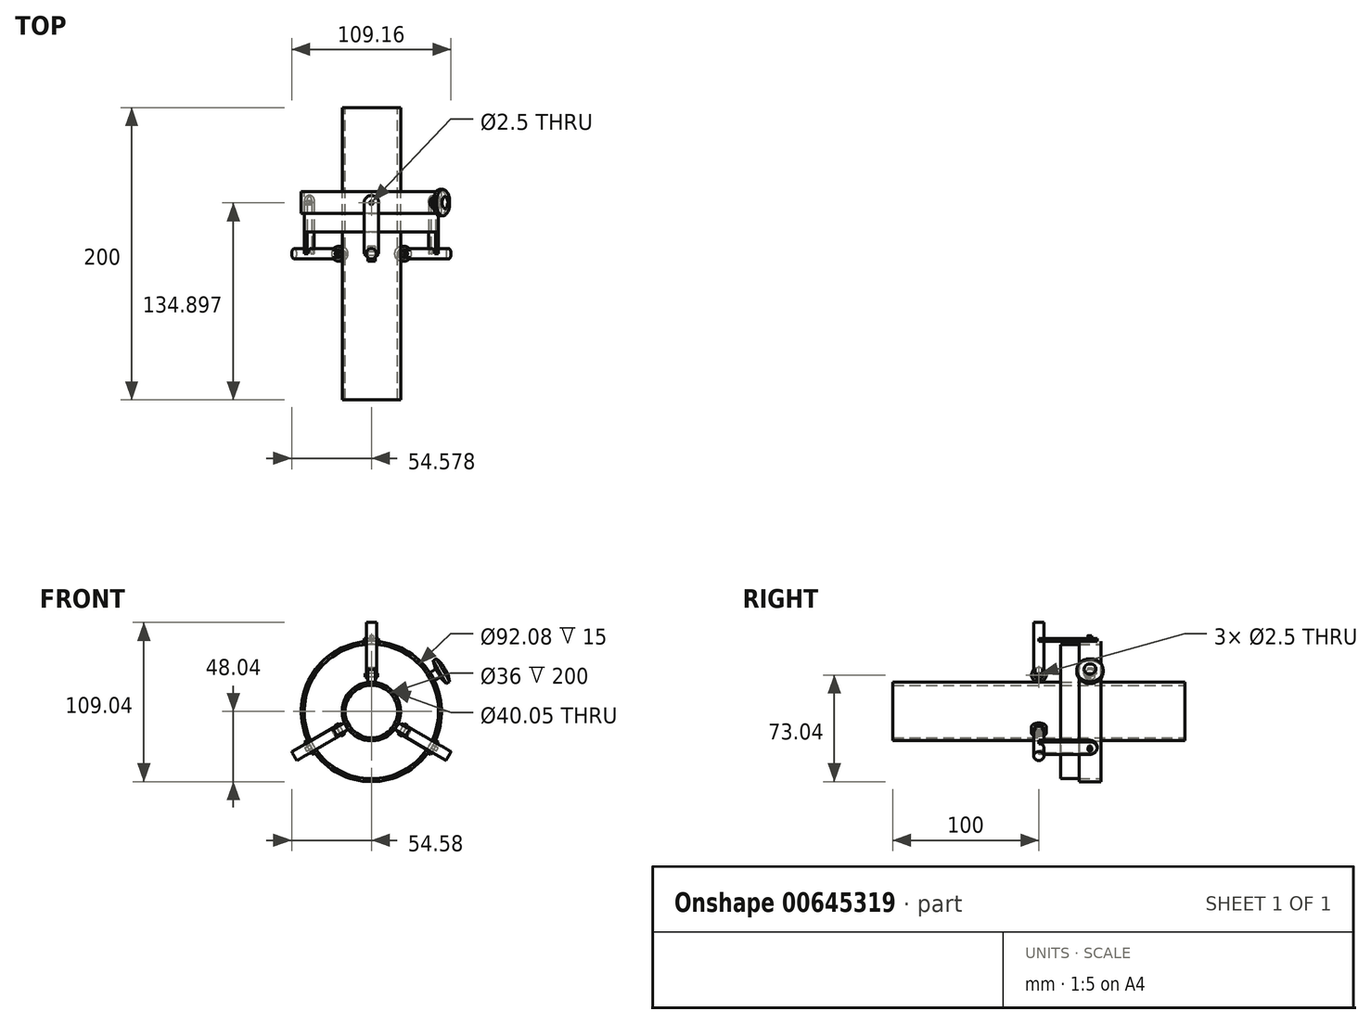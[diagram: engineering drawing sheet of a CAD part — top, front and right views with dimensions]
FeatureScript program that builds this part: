
annotation { "Feature Type Name" : "Feature", "Feature Type Description" : "" }
export const myFeature = defineFeature(function(context is Context, id is Id, definition is map)
    precondition{}
    {
        {
            var Q0;
            Q0=qCreatedBy(makeId("Front.planeOp"),FACE);
            var sketch = newSketch(context, id + "F0", { "sketchPlane" : qUnion([Q0])});
            skCircle(sketch, "E0", {"center": v(0, 0) * mm, "radius": 20 * mm});
            skCircle(sketch, "E1", {"center": v(0, 0) * mm, "radius": 18 * mm});
            skSolve(sketch);
        }
        {
            var Q0;
            Q0 = qSketchRegion(id + "F0", true);
            extrude(context, id + "F1", {"entities" : qUnion([Q0]), "depth" : 200 * mm, "offsetDistance" : 25 * mm, "symmetric" : true});
        }
        {
            var Q0;
            Q0=qCreatedBy(makeId("Right.planeOp"),FACE);
            var sketch = newSketch(context, id + "F2", { "sketchPlane" : qUnion([Q0])});
            skCircle(sketch, "E2", {"center": v(0, 25) * mm, "radius": 5 * mm});
            skCircle(sketch, "E3", {"center": v(0, 25) * mm, "radius": 1.25 * mm});
            skSolve(sketch);
        }
        {
            var Q0;
            Q0 = qSketchRegion(id + "F2", true);
            extrude(context, id + "F3", {"entities" : qUnion([Q0]), "depth" : 5 * mm, "offsetDistance" : 25 * mm, "symmetric" : true});
        }
        {
            var Q0;
            Q0=qCreatedBy(makeId("Right.planeOp"),FACE);
            var sketch = newSketch(context, id + "F4", { "sketchPlane" : qUnion([Q0])});
            skLineSegment(sketch, "E4.bottom", {"start": v(0, 21) * mm, "end": v(0.5, 21) * mm});
            skLineSegment(sketch, "E4.top", {"start": v(0, 61) * mm, "end": v(3.5, 61) * mm});
            skLineSegment(sketch, "E4.left", {"start": v(0, 21) * mm, "end": v(0, 61) * mm});
            skLineSegment(sketch, "E4.right", {"start": v(3.5, 24) * mm, "end": v(3.5, 61) * mm});
            skPoint(sketch, "E5.visualSharp", {"position": v(3.5, 21) * mm});
            skArc(sketch, "E5.filletArc", {"start": v(0.5, 21) * mm, "mid": v(2.62, 21.88) * mm, "end": v(3.5, 24) * mm});
            skSolve(sketch);
        }
        {
            var Q0;
            Q0 = qSketchRegion(id + "F4", true);
            var Q1;
            Q1=sQuery(id+"F4.wireOp",EDGE,"E4.left");
            revolve(context, id + "F5", {"entities" : qUnion([Q0]), "axis" : qUnion([Q1]), "revolveType" : RevolveType.FULL});
        }
        {
            var Q0;
            Q0=makeQuery(id+"F3.opExtrude","SWEPT_BODY",BODY,{"disambiguationData":[OSD([sQuery(id+"F2.wireOp",EDGE,"E2"),sQuery(id+"F2.wireOp",EDGE,"E3")])]});
            var Q1;
            Q1=makeQuery(id+"F5.opRevolve","SWEPT_BODY",BODY,{"disambiguationData":[OSD([sQuery(id+"F4.wireOp",EDGE,"E4.bottom"),sQuery(id+"F4.wireOp",EDGE,"E4.top"),sQuery(id+"F4.wireOp",EDGE,"E4.left"),sQuery(id+"F4.wireOp",EDGE,"E4.right"),sQuery(id+"F4.wireOp",EDGE,"E5.filletArc")])]});
            booleanBodies(context, id + "F6", {"operationType" : BooleanOperationType.SUBTRACTION, "tools" : qUnion([Q0]), "targets" : qUnion([Q1]), "keepTools" : true});
        }
        {
            var Q0;
            Q0=qCreatedBy(makeId("Right.planeOp"),FACE);
            var sketch = newSketch(context, id + "F7", { "sketchPlane" : qUnion([Q0])});
            skCircle(sketch, "E6", {"center": v(0, 25) * mm, "radius": 1.25 * mm});
            skSolve(sketch);
        }
        {
            var Q0;
            Q0 = qSketchRegion(id + "F7", true);
            extrude(context, id + "F8", {"entities" : qUnion([Q0]), "operationType" : NewBodyOperationType.REMOVE, "oppositeDirection" : true, "depth" : 25 * mm, "offsetDistance" : 25 * mm, "symmetric" : true});
        }
        {
            var Q0;
            Q0=qCreatedBy(makeId("Right.planeOp"),FACE);
            var sketch = newSketch(context, id + "F9", { "sketchPlane" : qUnion([Q0])});
            skCircle(sketch, "E7", {"center": v(0, 25) * mm, "radius": 1.25 * mm});
            skSolve(sketch);
        }
        {
            var Q0;
            Q0 = qSketchRegion(id + "F9", true);
            extrude(context, id + "F10", {"entities" : qUnion([Q0]), "depth" : 8.5 * mm, "offsetDistance" : 25 * mm, "symmetric" : true});
        }
        {
            var Q0;
            Q0=qCreatedBy(makeId("Front.planeOp"),FACE);
            var sketch = newSketch(context, id + "F11", { "sketchPlane" : qUnion([Q0])});
            skLineSegment(sketch, "E8.bottom", {"start": v(5, 50.04) * mm, "end": v(-5, 50.04) * mm});
            skLineSegment(sketch, "E8.top", {"start": v(5, 48.04) * mm, "end": v(-5, 48.04) * mm});
            skLineSegment(sketch, "E8.left", {"start": v(5, 50.04) * mm, "end": v(5, 48.04) * mm});
            skLineSegment(sketch, "E8.right", {"start": v(-5, 50.04) * mm, "end": v(-5, 48.04) * mm});
            skSolve(sketch);
        }
        {
            var Q0;
            Q0 = qSketchRegion(id + "F11", true);
            extrude(context, id + "F12", {"entities" : qUnion([Q0]), "operationType" : NewBodyOperationType.ADD, "oppositeDirection" : true, "depth" : 40 * mm, "offsetDistance" : 25 * mm});
        }
        {
            var Q0;
            Q0=makeQuery(id+"F12.opExtrude","SWEPT_FACE",FACE,{"disambiguationData":[OSD([sQuery(id+"F11.wireOp",EDGE,"E8.bottom")])]});
            var sketch = newSketch(context, id + "F13", { "sketchPlane" : qUnion([Q0])});
            skArc(sketch, "E9", {"start": v(5, 34.9) * mm, "mid": v(-0.1, 39.9) * mm, "end": v(-5, 34.72) * mm});
            skLineSegment(sketch, "E10", {"start": v(-5, 34.72) * mm, "end": v(-6.25, 34.72) * mm});
            skLineSegment(sketch, "E11", {"start": v(-6.25, 34.72) * mm, "end": v(-6.25, 41.57) * mm});
            skLineSegment(sketch, "E12", {"start": v(-6.25, 41.57) * mm, "end": v(6.15, 41.57) * mm});
            skLineSegment(sketch, "E13", {"start": v(6.15, 41.57) * mm, "end": v(6.15, 34.9) * mm});
            skLineSegment(sketch, "E14", {"start": v(6.15, 34.9) * mm, "end": v(5, 34.9) * mm});
            skCircle(sketch, "E15", {"center": v(0, 34.9) * mm, "radius": 1.25 * mm});
            skSolve(sketch);
        }
        {
            var Q0;
            Q0 = qSketchRegion(id + "F13", true);
            extrude(context, id + "F14", {"entities" : qUnion([Q0]), "operationType" : NewBodyOperationType.REMOVE, "oppositeDirection" : true, "depth" : 25 * mm, "offsetDistance" : 25 * mm});
        }
        {
            var Q0;
            Q0=makeQuery(id+"F3.opExtrude","SWEPT_BODY",BODY,{"disambiguationData":[OSD([sQuery(id+"F2.wireOp",EDGE,"E2"),sQuery(id+"F2.wireOp",EDGE,"E3")])]});
            var Q1;
            Q1=makeQuery(id+"F5.opRevolve","SWEPT_BODY",BODY,{"disambiguationData":[OSD([sQuery(id+"F4.wireOp",EDGE,"E4.bottom"),sQuery(id+"F4.wireOp",EDGE,"E4.top"),sQuery(id+"F4.wireOp",EDGE,"E4.left"),sQuery(id+"F4.wireOp",EDGE,"E4.right"),sQuery(id+"F4.wireOp",EDGE,"E5.filletArc")])]});
            var Q2;
            Q2=makeQuery(id+"F10.opExtrude","SWEPT_BODY",BODY,{"disambiguationData":[OSD([sQuery(id+"F9.wireOp",EDGE,"E7")])]});
            var Q3;
            Q3=makeQuery(id+"F1.opExtrude","CAP_EDGE",EDGE,{"disambiguationData":[OSD([sQuery(id+"F0.wireOp",EDGE,"E1")])],"isStart":false});
            circularPattern(context, id + "F15", {"entities" : qUnion([Q0, Q1, Q2]), "axis" : qUnion([Q3]), "angle" : 360 * degree, "instanceCount" : 3, "equalSpace" : true});
        }
        {
            var Q0;
            Q0=qCreatedBy(makeId("Front.planeOp"),FACE);
            cPlane(context, id + "F16", {"entities" : qUnion([Q0]), "cplaneType" : CPlaneType.OFFSET, "offset" : 35 * mm, "oppositeDirection" : true, "width" : 150 * mm, "height" : 150 * mm});
        }
        {
            var Q0;
            Q0=qCreatedBy(id+"F16.planeOp",FACE);
            var sketch = newSketch(context, id + "F17", { "sketchPlane" : qUnion([Q0])});
            skCircle(sketch, "E16", {"center": v(0, 0) * mm, "radius": 48.04 * mm});
            skCircle(sketch, "E17", {"center": v(0, 0) * mm, "radius": 46.04 * mm});
            skSolve(sketch);
        }
        {
            var Q0;
            Q0 = qSketchRegion(id + "F17", true);
            extrude(context, id + "F18", {"entities" : qUnion([Q0]), "depth" : 15 * mm, "offsetDistance" : 25 * mm, "symmetric" : true});
        }
        {
            var Q0;
            Q0=makeQuery(id+"F12.opExtrude","SWEPT_FACE",FACE,{"disambiguationData":[OSD([sQuery(id+"F11.wireOp",EDGE,"E8.bottom")])]});
            var sketch = newSketch(context, id + "F19", { "sketchPlane" : qUnion([Q0])});
            skCircle(sketch, "E18", {"center": v(0, 34.9) * mm, "radius": 1.25 * mm});
            skSolve(sketch);
        }
        {
            var Q0;
            Q0 = qSketchRegion(id + "F19", true);
            extrude(context, id + "F20", {"entities" : qUnion([Q0]), "depth" : 4 * mm, "offsetDistance" : 25 * mm, "symmetric" : true});
        }
        {
            var Q0;
            Q0=makeQuery(id+"F20.opExtrude","SWEPT_BODY",BODY,{"disambiguationData":[OSD([sQuery(id+"F19.wireOp",EDGE,"E18")])]});
            var Q1;
            Q1=makeQuery(id+"F1.opExtrude","CAP_EDGE",EDGE,{"disambiguationData":[OSD([sQuery(id+"F0.wireOp",EDGE,"E1")])],"isStart":true});
            circularPattern(context, id + "F21", {"entities" : qUnion([Q0]), "axis" : qUnion([Q1]), "angle" : 360 * degree, "instanceCount" : 3, "equalSpace" : true});
        }
        {
            var Q0;
            Q0=qCreatedBy(id+"F16.planeOp",FACE);
            var sketch = newSketch(context, id + "F22", { "sketchPlane" : qUnion([Q0])});
            skCircle(sketch, "E19", {"center": v(0, 0) * mm, "radius": 20.02 * mm});
            skCircle(sketch, "E20", {"center": v(0, 0) * mm, "radius": 45.98 * mm});
            skSolve(sketch);
        }
        {
            var Q0;
            Q0 = qSketchRegion(id + "F22", true);
            extrude(context, id + "F23", {"entities" : qUnion([Q0]), "depth" : 20 * mm, "offsetDistance" : 25 * mm, "hasSecondDirection" : true, "secondDirectionOppositeDirection" : true, "secondDirectionDepth" : 7.5 * mm});
        }
        {
            var Q0;
            Q0=qCreatedBy(id+"F16.planeOp",FACE);
            var sketch = newSketch(context, id + "F24", { "sketchPlane" : qUnion([Q0])});
            skLineSegment(sketch, "E21", {"start": v(0, 0) * mm, "end": v(72.35, 41.77) * mm, "construction": true});
            skLineSegment(sketch, "E22", {"start": v(41.6, 24.02) * mm, "end": v(50.4, 29.1) * mm});
            skLineSegment(sketch, "E23", {"start": v(50.4, 29.1) * mm, "end": v(48.35, 32.64) * mm});
            skLineSegment(sketch, "E24", {"start": v(48.35, 32.64) * mm, "end": v(44.51, 36.16) * mm});
            skLineSegment(sketch, "E25", {"start": v(44.51, 36.16) * mm, "end": v(42.3, 34.88) * mm});
            skLineSegment(sketch, "E26", {"start": v(42.3, 34.88) * mm, "end": v(43.59, 30.07) * mm});
            skLineSegment(sketch, "E27", {"start": v(43.59, 30.07) * mm, "end": v(44.15, 29.1) * mm});
            skLineSegment(sketch, "E28", {"start": v(44.15, 29.1) * mm, "end": v(40.1, 26.76) * mm});
            skLineSegment(sketch, "E29", {"start": v(40.1, 26.76) * mm, "end": v(41.6, 24.02) * mm});
            skSolve(sketch);
        }
        {
            var Q0;
            Q0 = qSketchRegion(id + "F24", true);
            var Q1;
            Q1=sQuery(id+"F24.wireOp",EDGE,"E22");
            revolve(context, id + "F25", {"entities" : qUnion([Q0]), "axis" : qUnion([Q1]), "revolveType" : RevolveType.FULL});
        }
    });
